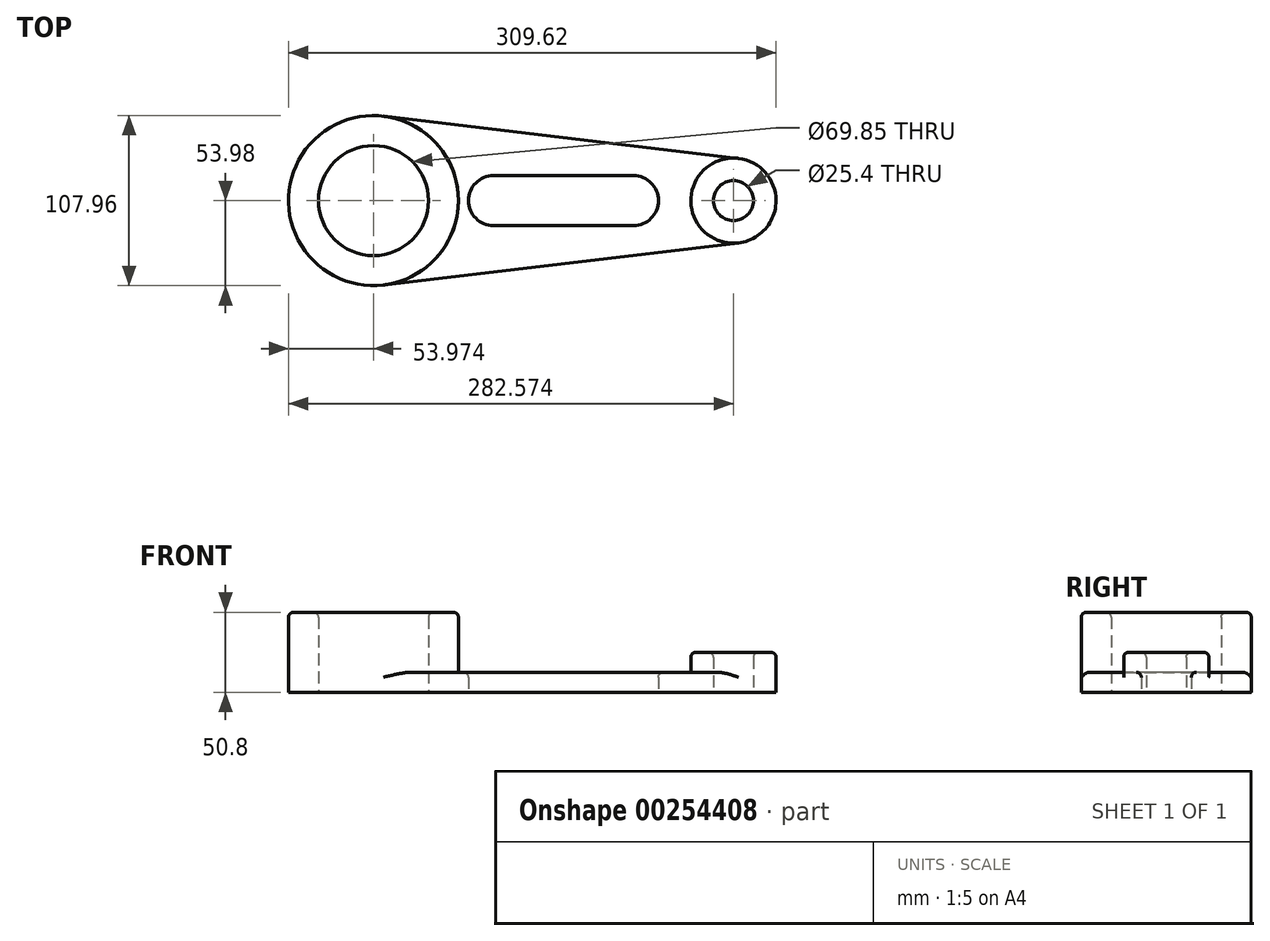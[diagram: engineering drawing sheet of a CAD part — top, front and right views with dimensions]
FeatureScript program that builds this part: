
annotation { "Feature Type Name" : "Feature", "Feature Type Description" : "" }
export const myFeature = defineFeature(function(context is Context, id is Id, definition is map)
    precondition{}
    {
        {
            var Q0;
            Q0=qCreatedBy(makeId("Top.planeOp"),FACE);
            var sketch = newSketch(context, id + "F0", { "sketchPlane" : qUnion([Q0])});
            skCircle(sketch, "E0", {"center": v(-88.52, 0) * mm, "radius": 34.93 * mm});
            skCircle(sketch, "E1", {"center": v(-88.52, 0) * mm, "radius": 53.98 * mm});
            skCircle(sketch, "E2", {"center": v(140.08, 0) * mm, "radius": 12.7 * mm});
            skCircle(sketch, "E3", {"center": v(140.08, 0) * mm, "radius": 27.05 * mm});
            skLineSegment(sketch, "E4", {"start": v(-82.16, 53.6) * mm, "end": v(143.27, 26.86) * mm});
            skLineSegment(sketch, "E5", {"start": v(-82.16, -53.6) * mm, "end": v(143.27, -26.86) * mm});
            skLineSegment(sketch, "E6", {"start": v(-88.52, 0) * mm, "end": v(140.08, 0) * mm});
            skLineSegment(sketch, "E7", {"start": v(-88.52, 0) * mm, "end": v(-12.32, 0) * mm});
            skArc(sketch, "E8", {"start": v(-12.32, 15.88) * mm, "mid": v(-28.2, 0) * mm, "end": v(-12.32, -15.88) * mm});
            skLineSegment(sketch, "E9", {"start": v(-12.32, 15.88) * mm, "end": v(76.58, 15.88) * mm});
            skLineSegment(sketch, "E10", {"start": v(-12.32, -15.88) * mm, "end": v(76.58, -15.88) * mm});
            skArc(sketch, "E11", {"start": v(76.58, 15.88) * mm, "mid": v(92.46, 0) * mm, "end": v(76.58, -15.88) * mm});
            skSolve(sketch);
        }
        {
            var Q0;
            Q0=makeQuery(id+"F0.imprint","IMPRINT",FACE,{"disambiguationData":[TD([[makeQuery(id+"F0.imprint","IMPRINT",EDGE,{"derivedFrom":sQuery(id+"F0.wireOp",EDGE,"E0")}),-1.0]])]});
            extrude(context, id + "F1", {"entities" : qUnion([Q0]), "depth" : 50.8 * mm});
        }
        {
            var Q0;
            Q0=makeQuery(id+"F0.imprint","IMPRINT",FACE,{"disambiguationData":[TD([[makeQuery(id+"F0.imprint","IMPRINT",EDGE,{"derivedFrom":sQuery(id+"F0.wireOp",EDGE,"E2")}),-1.0]])]});
            extrude(context, id + "F2", {"entities" : qUnion([Q0]), "depth" : 25.4 * mm});
        }
        {
            var Q0;
            {var subQ5=sQuery(id+"F0.wireOp",EDGE,"E4");Q0=makeQuery(id+"F0.imprint","IMPRINT",FACE,{"disambiguationData":[TD([[makeQuery(id+"F0.imprint","IMPRINT",EDGE,{"derivedFrom":subQ5}),-1.0]])]});}
            var Q1;
            {var subQ5=sQuery(id+"F0.wireOp",EDGE,"E5");Q1=makeQuery(id+"F0.imprint","IMPRINT",FACE,{"disambiguationData":[TD([[makeQuery(id+"F0.imprint","IMPRINT",EDGE,{"derivedFrom":subQ5}),1.0]])]});}
            extrude(context, id + "F3", {"entities" : qUnion([Q0, Q1]), "operationType" : NewBodyOperationType.ADD, "depth" : 12.7 * mm});
        }
        {
            var Q0;
            Q0=makeQuery(id+"F1.opExtrude","CAP_EDGE",EDGE,{"disambiguationData":[OSD([sQuery(id+"F0.wireOp",EDGE,"E1")])],"isStart":false});
            var Q1;
            Q1=makeQuery(id+"F1.opExtrude","CAP_EDGE",EDGE,{"disambiguationData":[OSD([sQuery(id+"F0.wireOp",EDGE,"E0")])],"isStart":false});
            var Q2;
            Q2=makeQuery(id+"F3.opExtrude","CAP_EDGE",EDGE,{"disambiguationData":[OSD([sQuery(id+"F0.wireOp",EDGE,"E8")])],"isStart":false});
            var Q3;
            Q3=makeQuery(id+"F3.opExtrude","CAP_EDGE",EDGE,{"disambiguationData":[OSD([sQuery(id+"F0.wireOp",EDGE,"E10")])],"isStart":false});
            var Q4;
            Q4=makeQuery(id+"F3.opExtrude","CAP_EDGE",EDGE,{"disambiguationData":[OSD([sQuery(id+"F0.wireOp",EDGE,"E11")])],"isStart":false});
            var Q5;
            Q5=makeQuery(id+"F3.opExtrude","CAP_EDGE",EDGE,{"disambiguationData":[OSD([sQuery(id+"F0.wireOp",EDGE,"E9")])],"isStart":false});
            var Q6;
            Q6=makeQuery(id+"F2.opExtrude","CAP_EDGE",EDGE,{"disambiguationData":[OSD([sQuery(id+"F0.wireOp",EDGE,"E2")])],"isStart":false});
            var Q7;
            Q7=makeQuery(id+"F2.opExtrude","CAP_EDGE",EDGE,{"disambiguationData":[OSD([sQuery(id+"F0.wireOp",EDGE,"E3")])],"isStart":false});
            var Q8;
            Q8=makeQuery(id+"F3.opExtrude","CAP_EDGE",EDGE,{"disambiguationData":[OSD([sQuery(id+"F0.wireOp",EDGE,"E5")])],"isStart":false});
            var Q9;
            Q9=makeQuery(id+"F3.opExtrude","CAP_EDGE",EDGE,{"disambiguationData":[OSD([sQuery(id+"F0.wireOp",EDGE,"E4")])],"isStart":false});
            fillet(context, id + "F4", {"entities" : qUnion([Q0, Q1, Q2, Q3, Q4, Q5, Q6, Q7, Q8, Q9]), "radius" : 3.17 * mm, "tangentPropagation" : true, "allowEdgeOverflow" : false});
        }
    });
